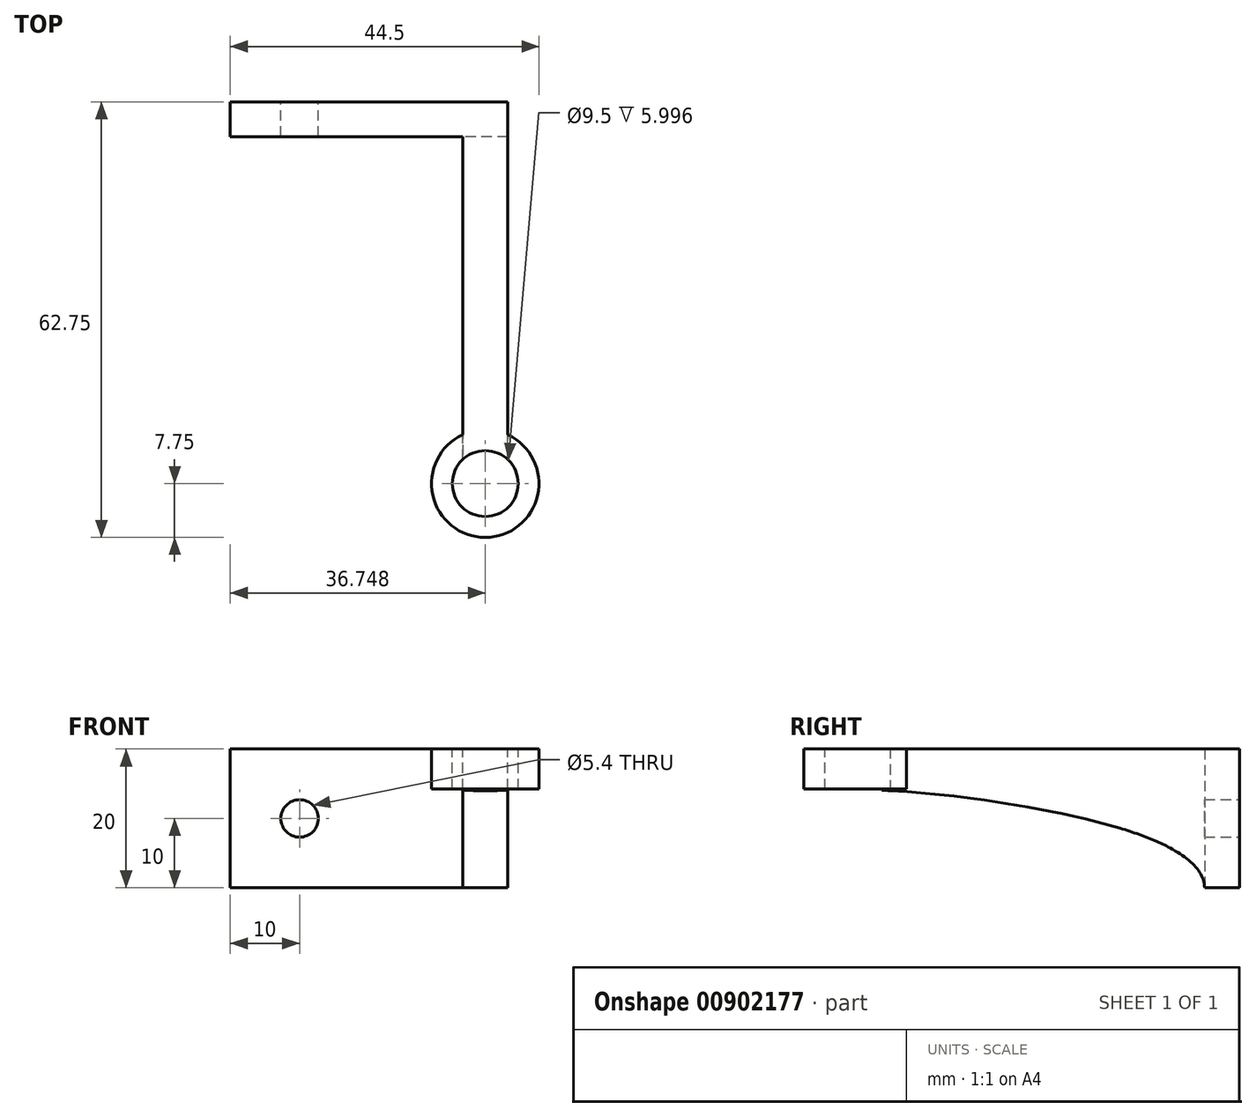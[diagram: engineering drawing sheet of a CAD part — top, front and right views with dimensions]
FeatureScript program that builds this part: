
annotation { "Feature Type Name" : "Feature", "Feature Type Description" : "" }
export const myFeature = defineFeature(function(context is Context, id is Id, definition is map)
    precondition{}
    {
        {
            var Q0;
            Q0=qCreatedBy(makeId("Front.planeOp"),FACE);
            var sketch = newSketch(context, id + "F0", { "sketchPlane" : qUnion([Q0])});
            skLineSegment(sketch, "E0.bottom", {"start": v(-10, 10) * mm, "end": v(30, 10) * mm});
            skLineSegment(sketch, "E0.top", {"start": v(-10, -10) * mm, "end": v(30, -10) * mm});
            skLineSegment(sketch, "E0.left", {"start": v(-10, 10) * mm, "end": v(-10, -10) * mm});
            skLineSegment(sketch, "E0.right", {"start": v(30, 10) * mm, "end": v(30, -10) * mm});
            skCircle(sketch, "E1", {"center": v(0, 0) * mm, "radius": 2.7 * mm});
            skSolve(sketch);
        }
        {
            var Q0;
            Q0=qSketchRegion(id+"F0",true);
            extrude(context, id + "F1", {"entities" : qUnion([Q0]), "depth" : 5 * mm, "offsetDistance" : 25 * mm});
        }
        {
            var Q0;
            Q0=makeQuery(id+"F1.opExtrude","CAP_FACE",FACE,{"disambiguationData":[OSD([sQuery(id+"F0.wireOp",EDGE,"E0.bottom"),sQuery(id+"F0.wireOp",EDGE,"E0.top"),sQuery(id+"F0.wireOp",EDGE,"E0.left"),sQuery(id+"F0.wireOp",EDGE,"E0.right"),sQuery(id+"F0.wireOp",EDGE,"E1")])],"isStart":false});
            var sketch = newSketch(context, id + "F2", { "sketchPlane" : qUnion([Q0])});
            skLineSegment(sketch, "E2.bottom", {"start": v(30, 10) * mm, "end": v(23.5, 10) * mm});
            skLineSegment(sketch, "E2.top", {"start": v(30, -10) * mm, "end": v(23.5, -10) * mm});
            skLineSegment(sketch, "E2.left", {"start": v(30, 10) * mm, "end": v(30, -10) * mm});
            skLineSegment(sketch, "E2.right", {"start": v(23.5, 10) * mm, "end": v(23.5, -10) * mm});
            skSolve(sketch);
        }
        {
            var Q0;
            Q0=makeQuery(id+"F2.imprint","IMPRINT",FACE,{"disambiguationData":[TD([[makeQuery(id+"F2.imprint","IMPRINT",EDGE,{"derivedFrom":sQuery(id+"F2.wireOp",EDGE,"E2.bottom")}),-1.0]])]});
            extrude(context, id + "F3", {"entities" : qUnion([Q0]), "operationType" : NewBodyOperationType.ADD, "depth" : 50 * mm, "offsetDistance" : 25 * mm});
        }
        {
            var Q0;
            Q0=makeQuery(id+"F3.opExtrude","SWEPT_FACE",FACE,{"disambiguationData":[OSD([sQuery(id+"F2.wireOp",EDGE,"E2.right")])]});
            var sketch = newSketch(context, id + "F4", { "sketchPlane" : qUnion([Q0])});
            skCircle(sketch, "E3", {"center": v(12.46, 0) * mm, "radius": 4.93 * mm});
            skFitSpline(sketch, "E4", {"points": [v(5, -10) * mm, v(27.89, 1.16) * mm, v(55, 4.23) * mm], "startDerivative": vector(1.23, 35.13) * mm, "endDerivative": vector(42.07, 1.5) * mm});
            skLineSegment(sketch, "E5", {"start": v(5, -10) * mm, "end": v(55, -10) * mm});
            skLineSegment(sketch, "E6", {"start": v(55, -10) * mm, "end": v(55, 4.23) * mm});
            skSolve(sketch);
        }
        {
            var Q0;
            Q0=makeQuery(id+"F4.imprint","IMPRINT",FACE,{"disambiguationData":[TD([[makeQuery(id+"F4.imprint","IMPRINT",EDGE,{"derivedFrom":sQuery(id+"F4.wireOp",EDGE,"E4")}),-1.0]])]});
            var Q1;
            {var subQ0=sQuery(id+"F4.wireOp",EDGE,"E4");var subQ1=sQuery(id+"F4.wireOp",EDGE,"E3");var subQ2=makeQuery(id+"F4.imprint","INTERSECT",VERTEX,{"disambiguationData":[OD(0.0)],"derivedFrom":[subQ1,subQ0]});Q1=makeQuery(id+"F4.imprint","IMPRINT",FACE,{"disambiguationData":[TD([[makeQuery(id+"F4.imprint","IMPRINT",EDGE,{"disambiguationData":[TD([[subQ2,-1.0]])],"derivedFrom":subQ1}),1.0]])]});}
            extrude(context, id + "F5", {"entities" : qUnion([Q0, Q1]), "operationType" : NewBodyOperationType.REMOVE, "oppositeDirection" : true, "depth" : 25 * mm, "offsetDistance" : 25 * mm});
        }
        {
            var Q0;
            Q0=makeQuery(id+"F3.boolean.opBoolean","MERGE",FACE,{"derivedFrom":[makeQuery(id+"F1.opExtrude","SWEPT_FACE",FACE,{"disambiguationData":[OSD([sQuery(id+"F0.wireOp",EDGE,"E0.bottom")])]}),makeQuery(id+"F3.opExtrude","SWEPT_FACE",FACE,{"disambiguationData":[OSD([sQuery(id+"F2.wireOp",EDGE,"E2.bottom")])]})]});
            var sketch = newSketch(context, id + "F6", { "sketchPlane" : qUnion([Q0])});
            skCircle(sketch, "E7", {"center": v(26.75, -55) * mm, "radius": 7.75 * mm});
            skCircle(sketch, "E8", {"center": v(26.75, -55) * mm, "radius": 4.75 * mm});
            skSolve(sketch);
        }
        {
            var Q0;
            {var subQ0=sQuery(id+"F2.wireOp",EDGE,"E2.bottom");var subQ3=makeQuery(id+"F3.opExtrude","CAP_EDGE",EDGE,{"disambiguationData":[OSD([subQ0])],"isStart":false});var subQ5=sQuery(id+"F6.wireOp",EDGE,"E8");var subQ6=makeQuery(id+"F6.imprint","INTERSECT",VERTEX,{"disambiguationData":[OD(0.0)],"derivedFrom":[subQ3,subQ5]});Q0=makeQuery(id+"F6.imprint","IMPRINT",FACE,{"disambiguationData":[TD([[makeQuery(id+"F6.imprint","IMPRINT",EDGE,{"disambiguationData":[TD([[subQ6,1.0]])],"derivedFrom":subQ5}),-1.0]])]});}
            var Q1;
            {var subQ0=sQuery(id+"F2.wireOp",EDGE,"E2.bottom");var subQ3=makeQuery(id+"F3.opExtrude","CAP_EDGE",EDGE,{"disambiguationData":[OSD([subQ0])],"isStart":false});var subQ5=sQuery(id+"F6.wireOp",EDGE,"E8");var subQ6=makeQuery(id+"F6.imprint","INTERSECT",VERTEX,{"disambiguationData":[OD(0.0)],"derivedFrom":[subQ3,subQ5]});Q1=makeQuery(id+"F6.imprint","IMPRINT",FACE,{"disambiguationData":[TD([[makeQuery(id+"F6.imprint","IMPRINT",EDGE,{"disambiguationData":[TD([[subQ6,-1.0]])],"derivedFrom":subQ5}),-1.0]])]});}
            var Q2;
            Q2=makeQuery(id+"F5.boolean.opBoolean","COPY",VERTEX,{"derivedFrom":makeQuery(id+"F5.opExtrude","CAP_VERTEX",VERTEX,{"disambiguationData":[OSD([sQuery(id+"F2.wireOp",EDGE,"E2.right"),sQuery(id+"F4.wireOp",EDGE,"E4"),sQuery(id+"F4.wireOp",EDGE,"E6")])],"isStart":true})});
            extrude(context, id + "F7", {"entities" : qUnion([Q0, Q1]), "operationType" : NewBodyOperationType.ADD, "endBound" : BoundingType.UP_TO_VERTEX, "oppositeDirection" : true, "depth" : 10 * mm, "endBoundEntityVertex" : qUnion([Q2]), "offsetDistance" : 25 * mm});
        }
        {
            var Q0;
            {var subQ0=sQuery(id+"F6.wireOp",EDGE,"E8");var subQ1=makeQuery(id+"F3.opExtrude","CAP_EDGE",EDGE,{"disambiguationData":[OSD([sQuery(id+"F2.wireOp",EDGE,"E2.bottom")])],"isStart":false});var subQ2=makeQuery(id+"F6.imprint","INTERSECT",VERTEX,{"disambiguationData":[OD(0.0)],"derivedFrom":[subQ1,subQ0]});Q0=makeQuery(id+"F6.imprint","IMPRINT",FACE,{"disambiguationData":[TD([[makeQuery(id+"F6.imprint","IMPRINT",EDGE,{"disambiguationData":[TD([[subQ2,-1.0]])],"derivedFrom":subQ0}),1.0]])]});}
            extrude(context, id + "F8", {"entities" : qUnion([Q0]), "operationType" : NewBodyOperationType.REMOVE, "oppositeDirection" : true, "depth" : 25 * mm, "offsetDistance" : 25 * mm});
        }
    });
